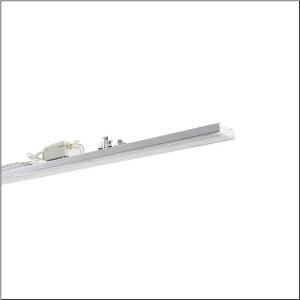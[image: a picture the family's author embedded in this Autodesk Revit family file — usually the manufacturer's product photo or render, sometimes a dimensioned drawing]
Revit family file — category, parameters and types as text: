
# Revit family: licross_r__21_recessed_ho_52tl11dn4e5s_92ad
name_source: partatom
category: Lighting Fixtures
units: mm (PartAtom-declared; Revit-internal decimal feet)

## family parameters
Cut with Voids When Loaded = No
Host = Face
Light Source = No
Part Type = Normal
Room Calculation Point = No
Round Connector Dimension = Use Diameter
Shared = No

## types (1)
- --- (1 x LED, 14970 lm, 84.6 W, 4000K)
    Apparent Load = 85 VA
    CIE Flux Codes = 87 95 99 100 100
    Color Rendering = 80
    Color Temperature = 4000K
    Default Elevation = 1800 mm
    Description = Licross® 21 Recessed HO, luminaire insert, of sheet steel, galvanised, coil coated, white, length: 1.500mm, width: 66mm, height: 67mm, LED rated luminous flux: 14.970lm, light colour: 840, control gear: DALI 2, with plug, 5-pole, with phase selection, mains connection: 220..240V, AC, 50/60Hz, rated input power: 85W, halogen-free wiring, primary light control with lens, of plastic, primary optical cover: cover, of PMMA, light emission: direct distribution, primary light characteristic: symmetric, protection rating (complete): IP40, insulation class (complete): insulation class I (protective earthing), certification: CE, ENEC, VDE, UKCA, protection symbol: D if used in an environment without relevant dust loads with corresponding accessories, impact resistance: IK06, permissible ambient temperature for indoor applications: -25..+30°C, corresponds to IFS (International Featured Standards) requirements for safety and quality in the food industry, reducing of maximum allowable ambient temperature of 5°C with ceiling mounting, LABS conformity tested according to VDMA 24364:2018-05, packaging unit: 1 piece
    Height = 58 mm
    Lamp = 1 x LED
    Lamp Light Flux = 14970 lm
    Lamp Power = 84.6 W
    Lamp count = 1
    Length = 1500 mm
    Luminous efficacy = 177 lm/W
    Manufacturer = Siteco
    ModVariant = No
    Model = 52TL11DN4E5S
    Mounting Place = Ceiling
    Mounting Type = Pendant
    Number of Poles = 1
    OnlyDefault = Yes
    Power Factor = 1
    Product Name = Licross® 21 Recessed HO
    Product group = luminaire insert
    ProductGroupID = 901
    Protection Class = Protection class I
    Protection Degree = IP 40
    RLX_Detail_Level = 1
    RLX_Emergency_Light_Flux = 0 lm
    RLX_Emergency_Type = 0
    RLX_Emergency_Type_DB = No
    RlxData = <blob elided: 24637 chars, md5=31644e4a>
    Socket = socket
    Standby Power = 0 W
    System Light Flux = 14970 lm
    System Power = 85 W
    Type Comments = factory setting: luminous flux: 100 % | dim-lin: 254 | 484 mA
    Type Image = l_1296930.jpg
    URL = http://relux.com
    VarID = @adj_058905
    Voltage = 0 V
    Weight = 0.00 kg
    Width = 66 mm

## geometry (parser evidence)
native form markers: Blend x4, Sweep x12
no freeform markers — native parametric forms only
